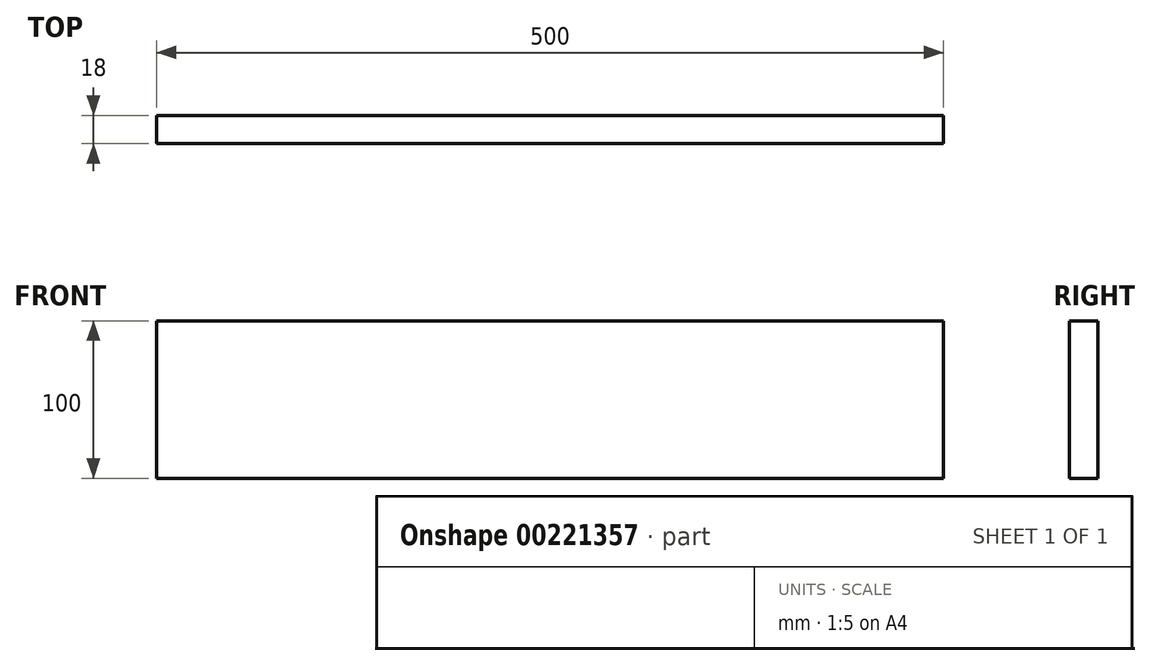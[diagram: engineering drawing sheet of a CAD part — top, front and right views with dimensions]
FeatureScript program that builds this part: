
annotation { "Feature Type Name" : "Feature", "Feature Type Description" : "" }
export const myFeature = defineFeature(function(context is Context, id is Id, definition is map)
    precondition{}
    {
        {
            var Q0;
            Q0=qCreatedBy(makeId("Front.planeOp"),FACE);
            var sketch = newSketch(context, id + "F0", { "sketchPlane" : qUnion([Q0])});
            skLineSegment(sketch, "E0.bottom", {"start": v(250, -50) * mm, "end": v(-250, -50) * mm});
            skLineSegment(sketch, "E0.top", {"start": v(250, 50) * mm, "end": v(-250, 50) * mm});
            skLineSegment(sketch, "E0.left", {"start": v(250, -50) * mm, "end": v(250, 50) * mm});
            skLineSegment(sketch, "E0.right", {"start": v(-250, -50) * mm, "end": v(-250, 50) * mm});
            skPoint(sketch, "E0.middle", {"position": v(0, 0) * mm});
            skSolve(sketch);
        }
        {
            var Q0;
            Q0 = qSketchRegion(id + "F0", true);
            extrude(context, id + "F1", {"entities" : qUnion([Q0]), "depth" : 18 * mm});
        }
    });
